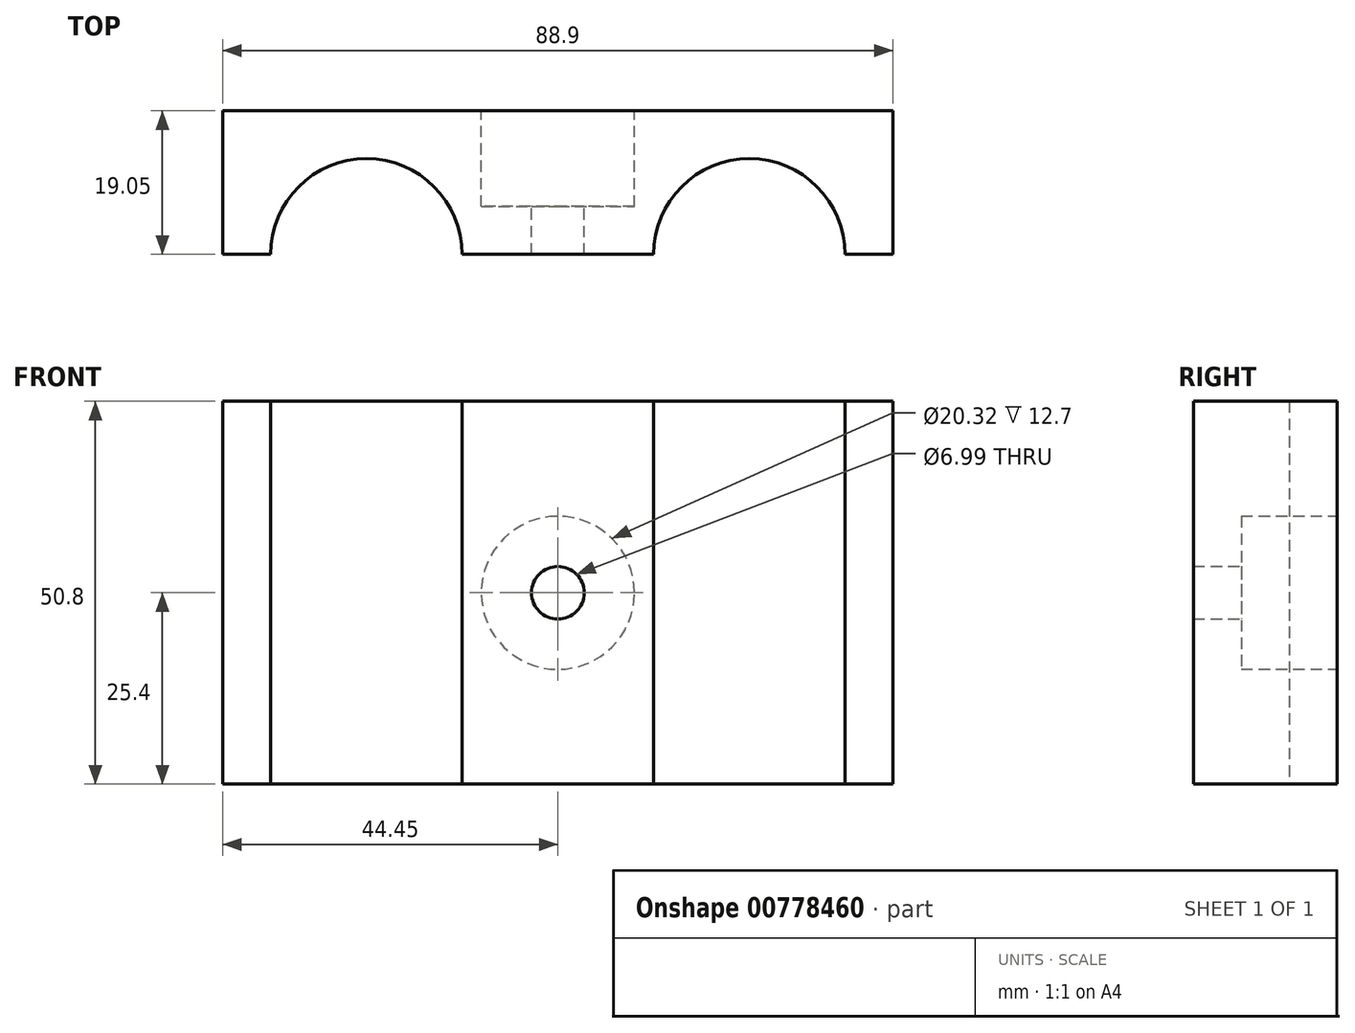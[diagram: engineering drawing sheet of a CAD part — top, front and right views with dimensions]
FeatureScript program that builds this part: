
annotation { "Feature Type Name" : "Feature", "Feature Type Description" : "" }
export const myFeature = defineFeature(function(context is Context, id is Id, definition is map)
    precondition{}
    {
        {
            var Q0;
            Q0=qCreatedBy(makeId("Top.planeOp"),FACE);
            var sketch = newSketch(context, id + "F0", { "sketchPlane" : qUnion([Q0])});
            skLineSegment(sketch, "E0.bottom", {"start": v(0, 0) * mm, "end": v(88.9, 0) * mm});
            skLineSegment(sketch, "E0.top", {"start": v(0, 19.05) * mm, "end": v(88.9, 19.05) * mm});
            skLineSegment(sketch, "E0.left", {"start": v(0, 0) * mm, "end": v(0, 19.05) * mm});
            skLineSegment(sketch, "E0.right", {"start": v(88.9, 0) * mm, "end": v(88.9, 19.05) * mm});
            skArc(sketch, "E1", {"start": v(31.75, 0) * mm, "mid": v(19.05, 12.7) * mm, "end": v(6.35, 0) * mm});
            skArc(sketch, "E2", {"start": v(82.55, 0) * mm, "mid": v(69.85, 12.7) * mm, "end": v(57.15, 0) * mm});
            skSolve(sketch);
        }
        {
            var Q0;
            Q0=makeQuery(id+"F0.imprint","IMPRINT",FACE,{"disambiguationData":[TD([[makeQuery(id+"F0.imprint","IMPRINT",EDGE,{"derivedFrom":sQuery(id+"F0.wireOp",EDGE,"E0.top")}),-1.0]])]});
            extrude(context, id + "F1", {"entities" : qUnion([Q0]), "depth" : 50.8 * mm, "offsetDistance" : 25.4 * mm});
        }
        {
            var Q0;
            Q0=makeQuery(id+"F1.opExtrude","SWEPT_FACE",FACE,{"disambiguationData":[OSD([sQuery(id+"F0.wireOp",EDGE,"E0.top")])]});
            var sketch = newSketch(context, id + "F2", { "sketchPlane" : qUnion([Q0])});
            skCircle(sketch, "E3", {"center": v(-44.45, 25.4) * mm, "radius": 10.16 * mm});
            skLineSegment(sketch, "E4", {"start": v(-88.9, 50.8) * mm, "end": v(0, 0) * mm, "construction": true});
            skSolve(sketch);
        }
        {
            var Q0;
            Q0 = qSketchRegion(id + "F2", true);
            extrude(context, id + "F3", {"entities" : qUnion([Q0]), "operationType" : NewBodyOperationType.REMOVE, "oppositeDirection" : true, "depth" : 12.7 * mm, "offsetDistance" : 25.4 * mm});
        }
        {
            var Q0;
            Q0=makeQuery(id+"F3.boolean.opBoolean","COPY",FACE,{"derivedFrom":makeQuery(id+"F3.opExtrude","CAP_FACE",FACE,{"disambiguationData":[OSD([sQuery(id+"F2.wireOp",EDGE,"E3")])],"isStart":false})});
            var sketch = newSketch(context, id + "F4", { "sketchPlane" : qUnion([Q0])});
            skCircle(sketch, "E5", {"center": v(-44.45, 25.4) * mm, "radius": 3.5 * mm});
            skSolve(sketch);
        }
        {
            var Q0;
            Q0 = qSketchRegion(id + "F4", true);
            extrude(context, id + "F5", {"entities" : qUnion([Q0]), "operationType" : NewBodyOperationType.REMOVE, "endBound" : BoundingType.THROUGH_ALL, "oppositeDirection" : true, "depth" : 25.4 * mm, "offsetDistance" : 25.4 * mm});
        }
    });
